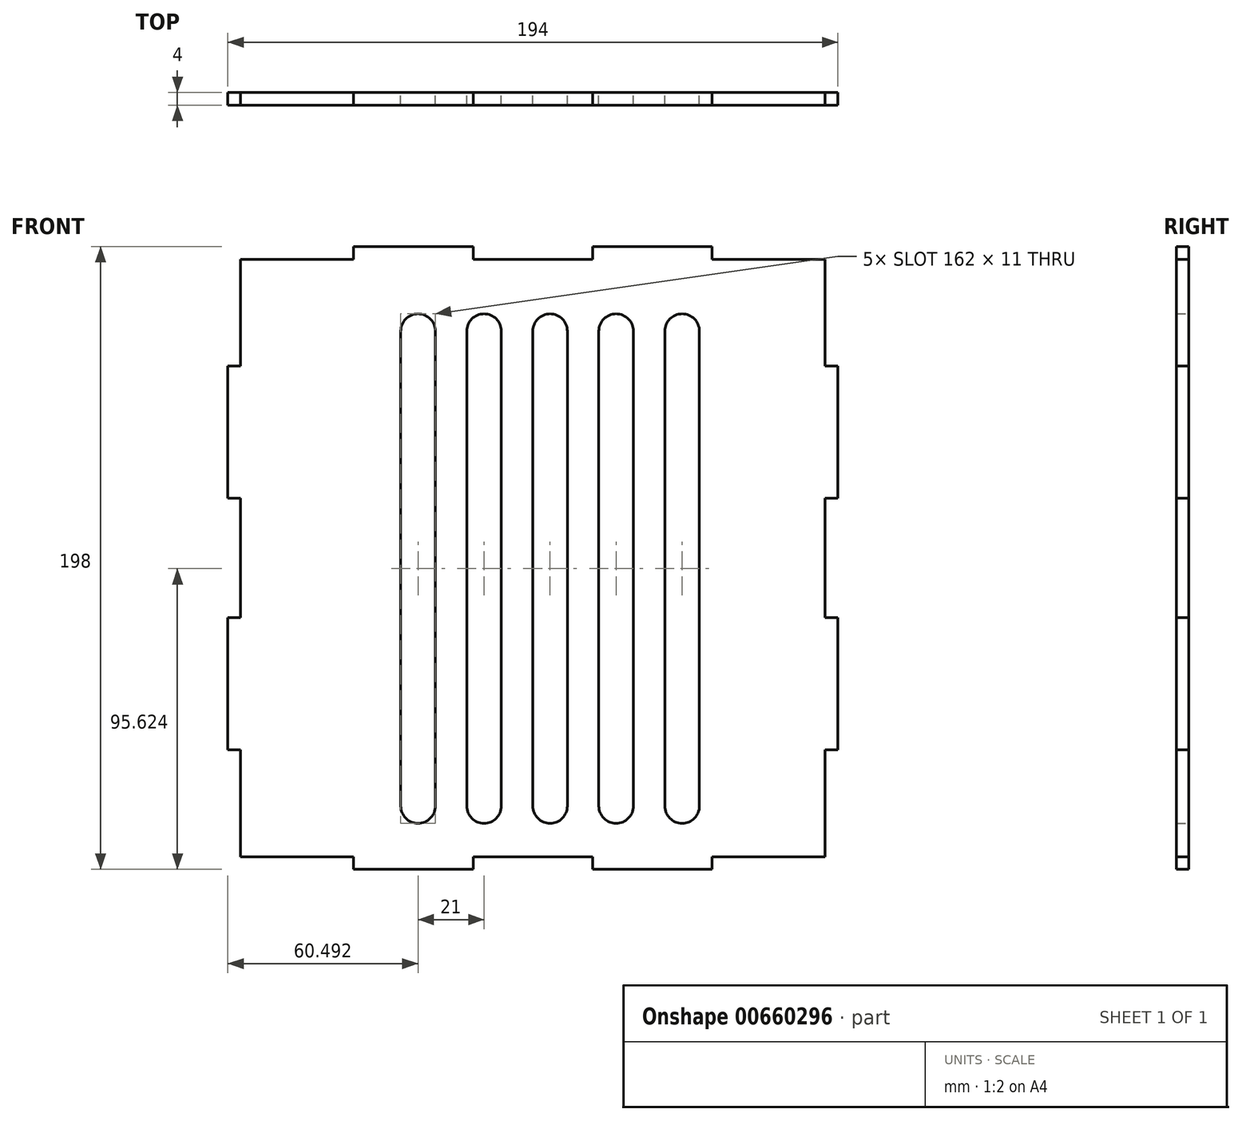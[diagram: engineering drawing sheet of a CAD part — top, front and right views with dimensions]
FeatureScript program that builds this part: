
annotation { "Feature Type Name" : "Feature", "Feature Type Description" : "" }
export const myFeature = defineFeature(function(context is Context, id is Id, definition is map)
    precondition{}
    {
        {
            var Q0;
            Q0=qCreatedBy(makeId("Front.planeOp"),FACE);
            var sketch = newSketch(context, id + "F0", { "sketchPlane" : qUnion([Q0])});
            skLineSegment(sketch, "E0.bottom", {"start": v(0, 0) * mm, "end": v(194, 0) * mm});
            skLineSegment(sketch, "E0.top", {"start": v(0, 198) * mm, "end": v(194, 198) * mm});
            skLineSegment(sketch, "E0.left", {"start": v(0, 0) * mm, "end": v(0, 198) * mm});
            skLineSegment(sketch, "E0.right", {"start": v(194, 0) * mm, "end": v(194, 198) * mm});
            skLineSegment(sketch, "E1.bottom", {"start": v(0, 0) * mm, "end": v(40, 0) * mm});
            skLineSegment(sketch, "E1.top", {"start": v(0, 4) * mm, "end": v(40, 4) * mm});
            skLineSegment(sketch, "E1.left", {"start": v(0, 0) * mm, "end": v(0, 4) * mm});
            skLineSegment(sketch, "E1.right", {"start": v(40, 0) * mm, "end": v(40, 4) * mm});
            skLineSegment(sketch, "E2.bottom", {"start": v(194, 0) * mm, "end": v(154, 0) * mm});
            skLineSegment(sketch, "E2.top", {"start": v(194, 4) * mm, "end": v(154, 4) * mm});
            skLineSegment(sketch, "E2.left", {"start": v(194, 0) * mm, "end": v(194, 4) * mm});
            skLineSegment(sketch, "E2.right", {"start": v(154, 0) * mm, "end": v(154, 4) * mm});
            skLineSegment(sketch, "E3.bottom", {"start": v(78, 0) * mm, "end": v(116, 0) * mm});
            skLineSegment(sketch, "E3.top", {"start": v(78, 4) * mm, "end": v(116, 4) * mm});
            skLineSegment(sketch, "E3.left", {"start": v(78, 0) * mm, "end": v(78, 4) * mm});
            skLineSegment(sketch, "E3.right", {"start": v(116, 0) * mm, "end": v(116, 4) * mm});
            skLineSegment(sketch, "E4.bottom", {"start": v(0, 198) * mm, "end": v(40, 198) * mm});
            skLineSegment(sketch, "E4.top", {"start": v(0, 194) * mm, "end": v(40, 194) * mm});
            skLineSegment(sketch, "E4.left", {"start": v(0, 198) * mm, "end": v(0, 194) * mm});
            skLineSegment(sketch, "E4.right", {"start": v(40, 198) * mm, "end": v(40, 194) * mm});
            skLineSegment(sketch, "E5.bottom", {"start": v(78, 198) * mm, "end": v(116, 198) * mm});
            skLineSegment(sketch, "E5.top", {"start": v(78, 194) * mm, "end": v(116, 194) * mm});
            skLineSegment(sketch, "E5.left", {"start": v(78, 198) * mm, "end": v(78, 194) * mm});
            skLineSegment(sketch, "E5.right", {"start": v(116, 198) * mm, "end": v(116, 194) * mm});
            skLineSegment(sketch, "E6.bottom", {"start": v(194, 198) * mm, "end": v(154, 198) * mm});
            skLineSegment(sketch, "E6.top", {"start": v(194, 194) * mm, "end": v(154, 194) * mm});
            skLineSegment(sketch, "E6.left", {"start": v(194, 198) * mm, "end": v(194, 194) * mm});
            skLineSegment(sketch, "E6.right", {"start": v(154, 198) * mm, "end": v(154, 194) * mm});
            skLineSegment(sketch, "E7.top", {"start": v(0, 80) * mm, "end": v(4, 80) * mm});
            skLineSegment(sketch, "E8.top", {"start": v(0, 118) * mm, "end": v(4, 118) * mm});
            skLineSegment(sketch, "E9.bottom", {"start": v(194, 80) * mm, "end": v(190, 80) * mm});
            skLineSegment(sketch, "E10.left", {"start": v(0, 118) * mm, "end": v(0, 80) * mm});
            skLineSegment(sketch, "E10.right", {"start": v(4, 118) * mm, "end": v(4, 80) * mm});
            skLineSegment(sketch, "E11.bottom", {"start": v(194, 118) * mm, "end": v(190, 118) * mm});
            skLineSegment(sketch, "E11.left", {"start": v(194, 118) * mm, "end": v(194, 80) * mm});
            skLineSegment(sketch, "E11.right", {"start": v(190, 118) * mm, "end": v(190, 80) * mm});
            skLineSegment(sketch, "E12.bottom", {"start": v(194, 0) * mm, "end": v(190, 0) * mm});
            skLineSegment(sketch, "E12.top", {"start": v(194, 38) * mm, "end": v(190, 38) * mm});
            skLineSegment(sketch, "E12.left", {"start": v(194, 0) * mm, "end": v(194, 38) * mm});
            skLineSegment(sketch, "E12.right", {"start": v(190, 0) * mm, "end": v(190, 38) * mm});
            skLineSegment(sketch, "E13.bottom", {"start": v(194, 198) * mm, "end": v(190, 198) * mm});
            skLineSegment(sketch, "E13.top", {"start": v(194, 160) * mm, "end": v(190, 160) * mm});
            skLineSegment(sketch, "E13.left", {"start": v(194, 198) * mm, "end": v(194, 160) * mm});
            skLineSegment(sketch, "E13.right", {"start": v(190, 198) * mm, "end": v(190, 160) * mm});
            skLineSegment(sketch, "E14.bottom", {"start": v(0, 198) * mm, "end": v(4, 198) * mm});
            skLineSegment(sketch, "E14.top", {"start": v(0, 160) * mm, "end": v(4, 160) * mm});
            skLineSegment(sketch, "E14.left", {"start": v(0, 198) * mm, "end": v(0, 160) * mm});
            skLineSegment(sketch, "E14.right", {"start": v(4, 198) * mm, "end": v(4, 160) * mm});
            skLineSegment(sketch, "E15.bottom", {"start": v(0, 0) * mm, "end": v(4, 0) * mm});
            skLineSegment(sketch, "E15.top", {"start": v(0, 38) * mm, "end": v(4, 38) * mm});
            skLineSegment(sketch, "E15.left", {"start": v(0, 0) * mm, "end": v(0, 38) * mm});
            skLineSegment(sketch, "E15.right", {"start": v(4, 0) * mm, "end": v(4, 38) * mm});
            skSolve(sketch);
        }
        {
            var Q0;
            {var subQ15=sQuery(id+"F0.wireOp",EDGE,"E1.right");Q0=makeQuery(id+"F0.imprint","IMPRINT",FACE,{"disambiguationData":[TD([[makeQuery(id+"F0.imprint","IMPRINT",EDGE,{"derivedFrom":subQ15}),-1.0]])]});}
            extrude(context, id + "F1", {"entities" : qUnion([Q0]), "depth" : 4 * mm, "offsetDistance" : 25 * mm});
        }
        {
            var Q0;
            Q0=qCreatedBy(makeId("Front.planeOp"),FACE);
            var sketch = newSketch(context, id + "F2", { "sketchPlane" : qUnion([Q0])});
            skLineSegment(sketch, "E16.bottom", {"start": v(55, 171.12) * mm, "end": v(66, 171.12) * mm});
            skLineSegment(sketch, "E16.top", {"start": v(55, 20.12) * mm, "end": v(66, 20.12) * mm});
            skLineSegment(sketch, "E16.left", {"start": v(55, 171.12) * mm, "end": v(55, 20.12) * mm});
            skLineSegment(sketch, "E16.right", {"start": v(66, 171.12) * mm, "end": v(66, 20.12) * mm});
            skLineSegment(sketch, "E17.bottom", {"start": v(76, 171.12) * mm, "end": v(87, 171.12) * mm});
            skLineSegment(sketch, "E17.top", {"start": v(76, 20.12) * mm, "end": v(87, 20.12) * mm});
            skLineSegment(sketch, "E17.left", {"start": v(76, 171.12) * mm, "end": v(76, 20.12) * mm});
            skLineSegment(sketch, "E17.right", {"start": v(87, 171.12) * mm, "end": v(87, 20.12) * mm});
            skLineSegment(sketch, "E18.bottom", {"start": v(97, 171.12) * mm, "end": v(108, 171.12) * mm});
            skLineSegment(sketch, "E18.top", {"start": v(97, 20.12) * mm, "end": v(108, 20.12) * mm});
            skLineSegment(sketch, "E18.left", {"start": v(97, 171.12) * mm, "end": v(97, 20.12) * mm});
            skLineSegment(sketch, "E18.right", {"start": v(108, 171.12) * mm, "end": v(108, 20.12) * mm});
            skLineSegment(sketch, "E19.bottom", {"start": v(118, 171.12) * mm, "end": v(129, 171.12) * mm});
            skLineSegment(sketch, "E19.top", {"start": v(118, 20.12) * mm, "end": v(129, 20.12) * mm});
            skLineSegment(sketch, "E19.left", {"start": v(118, 171.12) * mm, "end": v(118, 20.12) * mm});
            skLineSegment(sketch, "E19.right", {"start": v(129, 171.12) * mm, "end": v(129, 20.12) * mm});
            skLineSegment(sketch, "E20.bottom", {"start": v(139, 171.12) * mm, "end": v(150, 171.12) * mm});
            skLineSegment(sketch, "E20.top", {"start": v(139, 20.12) * mm, "end": v(150, 20.12) * mm});
            skLineSegment(sketch, "E20.left", {"start": v(139, 171.12) * mm, "end": v(139, 20.12) * mm});
            skLineSegment(sketch, "E20.right", {"start": v(150, 171.12) * mm, "end": v(150, 20.12) * mm});
            skArc(sketch, "E21", {"start": v(55, 20.12) * mm, "mid": v(60.5, 14.62) * mm, "end": v(66, 20.12) * mm});
            skArc(sketch, "E22", {"start": v(76, 20.12) * mm, "mid": v(81.5, 14.62) * mm, "end": v(87, 20.12) * mm});
            skArc(sketch, "E23", {"start": v(97, 20.12) * mm, "mid": v(102.5, 14.62) * mm, "end": v(108, 20.12) * mm});
            skArc(sketch, "E24", {"start": v(118, 20.12) * mm, "mid": v(123.5, 14.62) * mm, "end": v(129, 20.12) * mm});
            skArc(sketch, "E25", {"start": v(139, 20.12) * mm, "mid": v(144.5, 14.62) * mm, "end": v(150, 20.12) * mm});
            skArc(sketch, "E26", {"start": v(66, 171.12) * mm, "mid": v(60.5, 176.62) * mm, "end": v(55, 171.12) * mm});
            skArc(sketch, "E27", {"start": v(87, 171.12) * mm, "mid": v(81.5, 176.62) * mm, "end": v(76, 171.12) * mm});
            skArc(sketch, "E28", {"start": v(108, 171.12) * mm, "mid": v(102.5, 176.62) * mm, "end": v(97, 171.12) * mm});
            skArc(sketch, "E29", {"start": v(129, 171.12) * mm, "mid": v(123.5, 176.62) * mm, "end": v(118, 171.12) * mm});
            skArc(sketch, "E30", {"start": v(150, 171.12) * mm, "mid": v(144.5, 176.62) * mm, "end": v(139, 171.12) * mm});
            skSolve(sketch);
        }
        {
            var Q0;
            Q0 = qSketchRegion(id + "F2", true);
            extrude(context, id + "F3", {"entities" : qUnion([Q0]), "operationType" : NewBodyOperationType.REMOVE, "depth" : 4 * mm, "offsetDistance" : 25 * mm});
        }
    });
